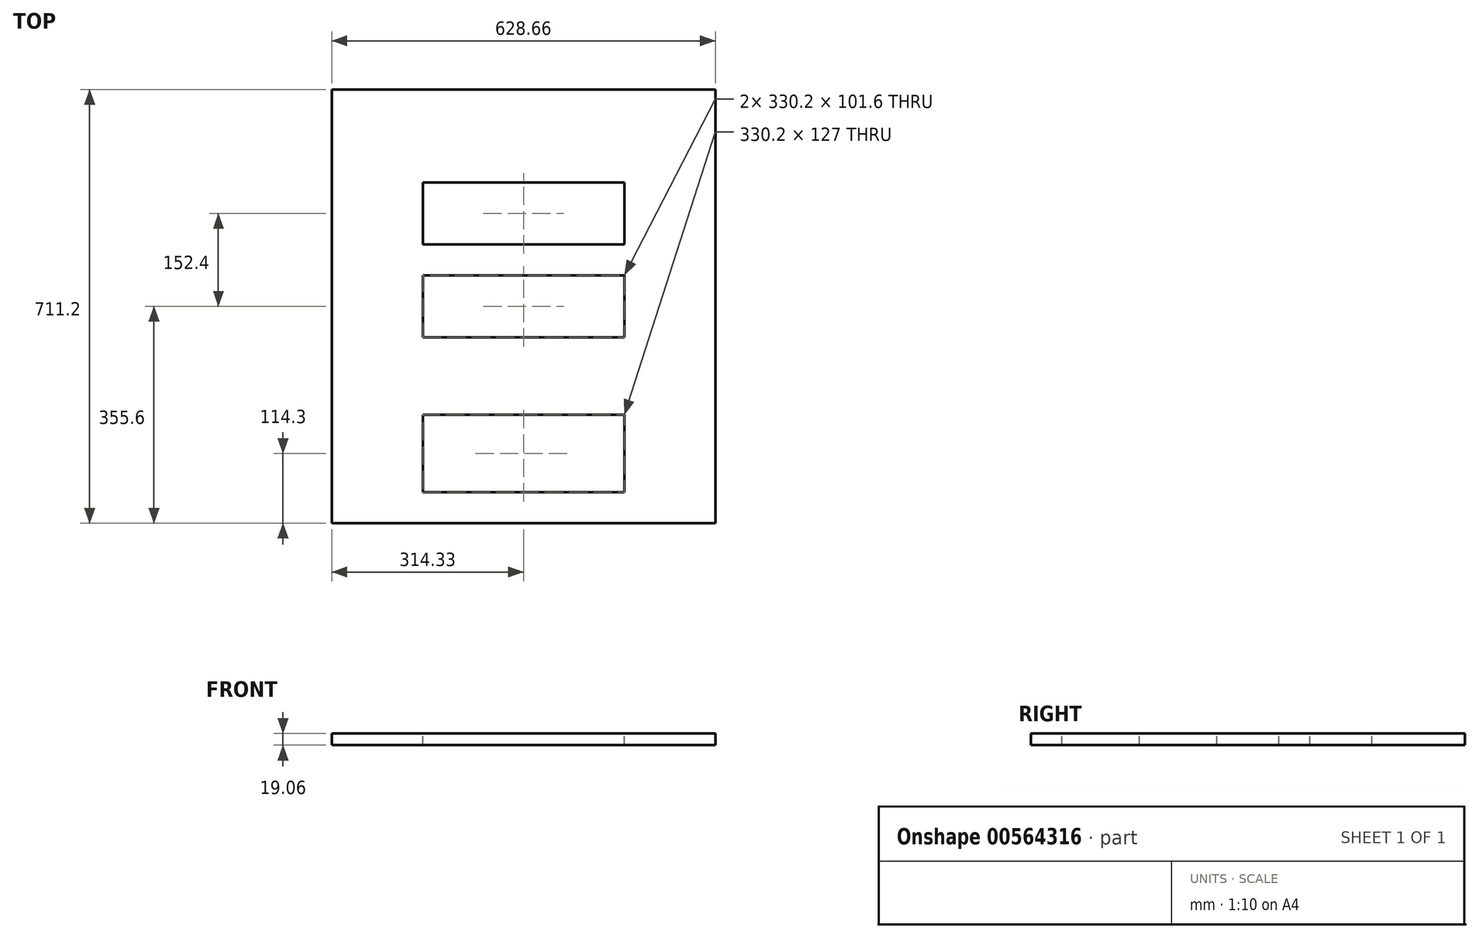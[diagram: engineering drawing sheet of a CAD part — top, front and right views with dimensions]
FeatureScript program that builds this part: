
annotation { "Feature Type Name" : "Feature", "Feature Type Description" : "" }
export const myFeature = defineFeature(function(context is Context, id is Id, definition is map)
    precondition{}
    {
        {
            var Q0;
            Q0=qCreatedBy(makeId("Front.planeOp"),FACE);
            var sketch = newSketch(context, id + "F0", { "sketchPlane" : qUnion([Q0])});
            skLineSegment(sketch, "E0.bottom", {"start": v(-314.32, 9.53) * mm, "end": v(314.33, 9.53) * mm});
            skLineSegment(sketch, "E0.top", {"start": v(-314.32, -9.52) * mm, "end": v(314.33, -9.52) * mm});
            skLineSegment(sketch, "E0.left", {"start": v(-314.32, 9.53) * mm, "end": v(-314.32, -9.52) * mm});
            skLineSegment(sketch, "E0.right", {"start": v(314.33, 9.53) * mm, "end": v(314.33, -9.52) * mm});
            skPoint(sketch, "E0.middle", {"position": v(0, 0) * mm});
            skSolve(sketch);
        }
        {
            var Q0;
            Q0 = qSketchRegion(id + "F0", true);
            extrude(context, id + "F1", {"entities" : qUnion([Q0]), "depth" : 711.2 * mm, "offsetDistance" : 25.4 * mm});
        }
        {
            var Q0;
            Q0=makeQuery(id+"F1.opExtrude","SWEPT_FACE",FACE,{"disambiguationData":[OSD([sQuery(id+"F0.wireOp",EDGE,"E0.bottom")])]});
            var sketch = newSketch(context, id + "F2", { "sketchPlane" : qUnion([Q0])});
            skLineSegment(sketch, "E1", {"start": v(0, -15.26) * mm, "end": v(0, -711.2) * mm, "construction": true});
            skPoint(sketch, "E1.startSnap0", {"position": v(0, 0) * mm});
            skLineSegment(sketch, "E2.bottom", {"start": v(-165.1, -152.4) * mm, "end": v(165.1, -152.4) * mm});
            skLineSegment(sketch, "E2.top", {"start": v(-165.1, -254) * mm, "end": v(165.1, -254) * mm});
            skLineSegment(sketch, "E2.left", {"start": v(-165.1, -152.4) * mm, "end": v(-165.1, -254) * mm});
            skLineSegment(sketch, "E2.right", {"start": v(165.1, -152.4) * mm, "end": v(165.1, -254) * mm});
            skPoint(sketch, "E2.middle", {"position": v(0, -203.2) * mm});
            skLineSegment(sketch, "E3.bottom", {"start": v(-165.1, -304.8) * mm, "end": v(165.1, -304.8) * mm});
            skLineSegment(sketch, "E3.top", {"start": v(-165.1, -406.4) * mm, "end": v(165.1, -406.4) * mm});
            skLineSegment(sketch, "E3.left", {"start": v(-165.1, -304.8) * mm, "end": v(-165.1, -406.4) * mm});
            skLineSegment(sketch, "E3.right", {"start": v(165.1, -304.8) * mm, "end": v(165.1, -406.4) * mm});
            skPoint(sketch, "E3.middle", {"position": v(0, -355.6) * mm});
            skLineSegment(sketch, "E4.bottom", {"start": v(-165.1, -660.4) * mm, "end": v(165.1, -660.4) * mm});
            skLineSegment(sketch, "E4.top", {"start": v(-165.1, -533.4) * mm, "end": v(165.1, -533.4) * mm});
            skLineSegment(sketch, "E4.left", {"start": v(-165.1, -660.4) * mm, "end": v(-165.1, -533.4) * mm});
            skLineSegment(sketch, "E4.right", {"start": v(165.1, -660.4) * mm, "end": v(165.1, -533.4) * mm});
            skPoint(sketch, "E4.middle", {"position": v(0, -596.9) * mm});
            skSolve(sketch);
        }
        {
            var Q0;
            Q0 = qSketchRegion(id + "F2", true);
            extrude(context, id + "F3", {"entities" : qUnion([Q0]), "operationType" : NewBodyOperationType.REMOVE, "oppositeDirection" : true, "depth" : 25.4 * mm, "offsetDistance" : 25.4 * mm});
        }
    });
